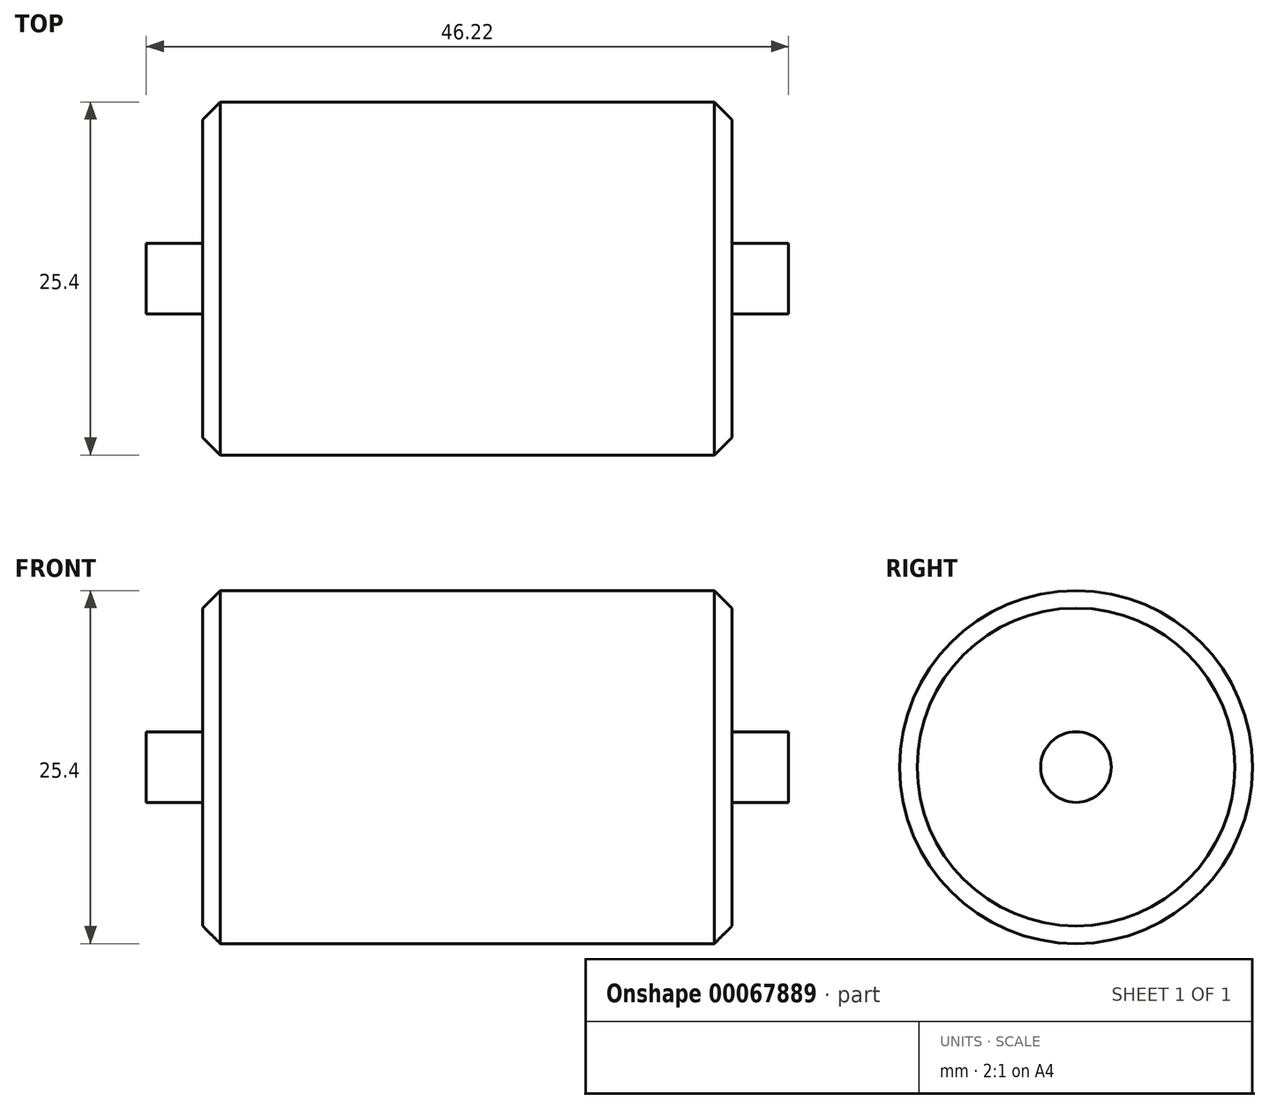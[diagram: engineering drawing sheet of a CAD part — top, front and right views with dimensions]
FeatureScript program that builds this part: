
annotation { "Feature Type Name" : "Feature", "Feature Type Description" : "" }
export const myFeature = defineFeature(function(context is Context, id is Id, definition is map)
    precondition{}
    {
        {
            var Q0;
            Q0=qCreatedBy(makeId("Right.planeOp"),FACE);
            var sketch = newSketch(context, id + "F0", { "sketchPlane" : qUnion([Q0])});
            skCircle(sketch, "E0", {"center": v(0, 0) * mm, "radius": 12.7 * mm});
            skSolve(sketch);
        }
        {
            var Q0;
            Q0=makeQuery(id+"F0.imprint","IMPRINT",FACE,{"disambiguationData":[TD([[makeQuery(id+"F0.imprint","IMPRINT",EDGE,{"derivedFrom":sQuery(id+"F0.wireOp",EDGE,"E0")}),1.0]])]});
            extrude(context, id + "F1", {"entities" : qUnion([Q0]), "depth" : 38.1 * mm});
        }
        {
            var Q0;
            Q0=makeQuery(id+"F1.opExtrude","CAP_EDGE",EDGE,{"disambiguationData":[OSD([sQuery(id+"F0.wireOp",EDGE,"E0")])],"isStart":true});
            var Q1;
            Q1=makeQuery(id+"F1.opExtrude","SWEPT_FACE",FACE,{"disambiguationData":[OSD([sQuery(id+"F0.wireOp",EDGE,"E0")])]});
            chamfer(context, id + "F2", {"entities" : qUnion([Q0, Q1]), "width" : 1.27 * mm, "tangentPropagation" : true});
        }
        {
            var Q0;
            Q0=makeQuery(id+"F1.opExtrude","CAP_FACE",FACE,{"disambiguationData":[OSD([sQuery(id+"F0.wireOp",EDGE,"E0")])],"isStart":false});
            var sketch = newSketch(context, id + "F3", { "sketchPlane" : qUnion([Q0])});
            skCircle(sketch, "E1", {"center": v(0, 0) * mm, "radius": 2.54 * mm});
            skSolve(sketch);
        }
        {
            var Q0;
            Q0=makeQuery(id+"F3.imprint","IMPRINT",FACE,{"disambiguationData":[TD([[makeQuery(id+"F3.imprint","IMPRINT",EDGE,{"derivedFrom":sQuery(id+"F3.wireOp",EDGE,"E1")}),1.0]])]});
            extrude(context, id + "F4", {"entities" : qUnion([Q0]), "operationType" : NewBodyOperationType.ADD, "depth" : 4.06 * mm});
        }
        {
            var Q0;
            Q0=makeQuery(id+"F1.opExtrude","CAP_FACE",FACE,{"disambiguationData":[OSD([sQuery(id+"F0.wireOp",EDGE,"E0")])],"isStart":true});
            var sketch = newSketch(context, id + "F5", { "sketchPlane" : qUnion([Q0])});
            skCircle(sketch, "E2", {"center": v(0, 0) * mm, "radius": 2.54 * mm});
            skSolve(sketch);
        }
        {
            var Q0;
            Q0=makeQuery(id+"F5.imprint","IMPRINT",FACE,{"disambiguationData":[TD([[makeQuery(id+"F5.imprint","IMPRINT",EDGE,{"derivedFrom":sQuery(id+"F5.wireOp",EDGE,"E2")}),1.0]])]});
            extrude(context, id + "F6", {"entities" : qUnion([Q0]), "operationType" : NewBodyOperationType.ADD, "depth" : 4.06 * mm});
        }
    });
